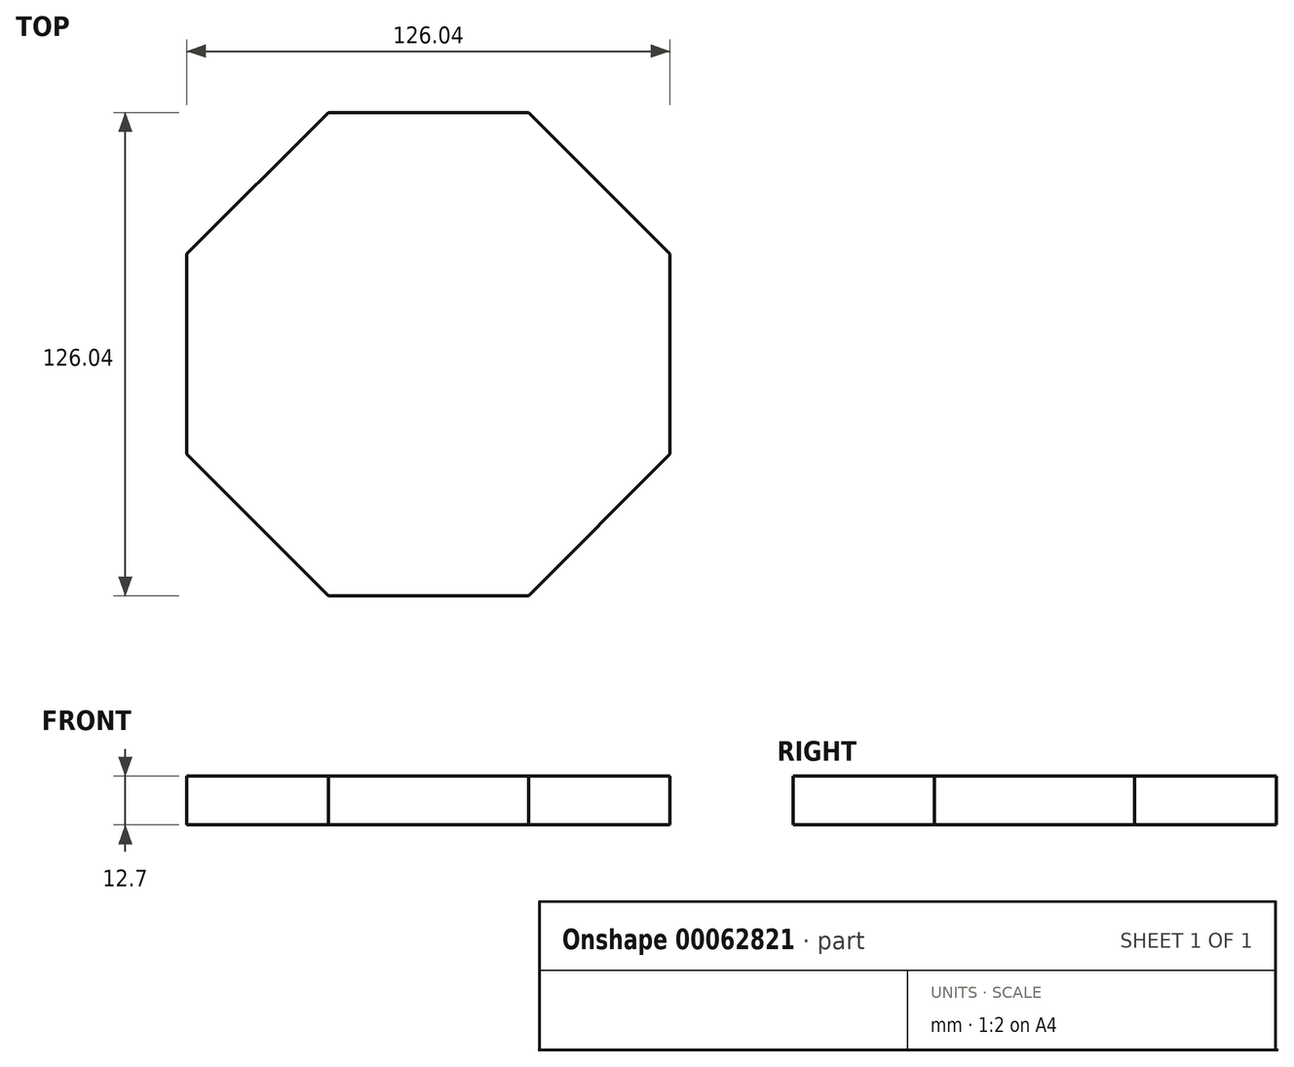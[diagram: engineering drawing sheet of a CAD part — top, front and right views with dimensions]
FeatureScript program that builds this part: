
annotation { "Feature Type Name" : "Feature", "Feature Type Description" : "" }
export const myFeature = defineFeature(function(context is Context, id is Id, definition is map)
    precondition{}
    {
        {
            var Q0;
            Q0=qCreatedBy(makeId("Top.planeOp"),FACE);
            var sketch = newSketch(context, id + "F0", { "sketchPlane" : qUnion([Q0])});
            skLineSegment(sketch, "E0.0", {"start": v(-26.1, 63.02) * mm, "end": v(26.1, 63.02) * mm});
            skLineSegment(sketch, "E0.1", {"start": v(26.1, 63.02) * mm, "end": v(63.02, 26.1) * mm});
            skLineSegment(sketch, "E0.2", {"start": v(63.02, 26.1) * mm, "end": v(63.02, -26.1) * mm});
            skLineSegment(sketch, "E0.3", {"start": v(63.02, -26.1) * mm, "end": v(26.1, -63.02) * mm});
            skLineSegment(sketch, "E0.4", {"start": v(26.1, -63.02) * mm, "end": v(-26.1, -63.02) * mm});
            skLineSegment(sketch, "E0.5", {"start": v(-26.1, -63.02) * mm, "end": v(-63.02, -26.1) * mm});
            skLineSegment(sketch, "E0.6", {"start": v(-63.02, -26.1) * mm, "end": v(-63.02, 26.1) * mm});
            skLineSegment(sketch, "E0.7", {"start": v(-63.02, 26.1) * mm, "end": v(-26.1, 63.02) * mm});
            skPoint(sketch, "E0.0.midPoint", {"position": v(0, 63.02) * mm});
            skLineSegment(sketch, "E1", {"start": v(0, 0) * mm, "end": v(26.1, 63.02) * mm});
            skLineSegment(sketch, "E2", {"start": v(0, 0) * mm, "end": v(-26.1, 63.02) * mm});
            skLineSegment(sketch, "E3", {"start": v(0, 0) * mm, "end": v(-63.02, 26.1) * mm});
            skLineSegment(sketch, "E4", {"start": v(0, 0) * mm, "end": v(-63.02, -26.1) * mm});
            skLineSegment(sketch, "E5", {"start": v(0, 0) * mm, "end": v(-26.1, -63.02) * mm});
            skLineSegment(sketch, "E6", {"start": v(0, 0) * mm, "end": v(26.1, -63.02) * mm});
            skLineSegment(sketch, "E7", {"start": v(0, 0) * mm, "end": v(63.02, -26.1) * mm});
            skLineSegment(sketch, "E8", {"start": v(0, 0) * mm, "end": v(63.02, 26.1) * mm});
            skPoint(sketch, "E9.centerSnap0", {"position": v(13.05, 31.5) * mm});
            skSolve(sketch);
        }
        {
            var Q0;
            {var subQ4=sQuery(id+"F0.wireOp",EDGE,"E0.5");Q0=makeQuery(id+"F0.imprint","IMPRINT",FACE,{"disambiguationData":[TD([[makeQuery(id+"F0.imprint","IMPRINT",EDGE,{"derivedFrom":subQ4}),-1.0]])]});}
            var Q1;
            {var subQ2=sQuery(id+"F0.wireOp",EDGE,"E0.0");Q1=makeQuery(id+"F0.imprint","IMPRINT",FACE,{"disambiguationData":[TD([[makeQuery(id+"F0.imprint","IMPRINT",EDGE,{"derivedFrom":subQ2}),-1.0]])]});}
            var Q2;
            {var subQ5=sQuery(id+"F0.wireOp",EDGE,"E0.1");Q2=makeQuery(id+"F0.imprint","IMPRINT",FACE,{"disambiguationData":[TD([[makeQuery(id+"F0.imprint","IMPRINT",EDGE,{"derivedFrom":subQ5}),-1.0]])]});}
            var Q3;
            {var subQ5=sQuery(id+"F0.wireOp",EDGE,"E0.2");Q3=makeQuery(id+"F0.imprint","IMPRINT",FACE,{"disambiguationData":[TD([[makeQuery(id+"F0.imprint","IMPRINT",EDGE,{"derivedFrom":subQ5}),-1.0]])]});}
            var Q4;
            {var subQ1=sQuery(id+"F0.wireOp",EDGE,"E0.3");Q4=makeQuery(id+"F0.imprint","IMPRINT",FACE,{"disambiguationData":[TD([[makeQuery(id+"F0.imprint","IMPRINT",EDGE,{"derivedFrom":subQ1}),-1.0]])]});}
            var Q5;
            Q5=makeQuery(id+"F0.imprint","IMPRINT",FACE,{"disambiguationData":[TD([[makeQuery(id+"F0.imprint","IMPRINT",EDGE,{"derivedFrom":sQuery(id+"F0.wireOp",EDGE,"E0.4")}),-1.0]])]});
            var Q6;
            {var subQ1=sQuery(id+"F0.wireOp",EDGE,"E0.6");Q6=makeQuery(id+"F0.imprint","IMPRINT",FACE,{"disambiguationData":[TD([[makeQuery(id+"F0.imprint","IMPRINT",EDGE,{"derivedFrom":subQ1}),-1.0]])]});}
            var Q7;
            {var subQ5=sQuery(id+"F0.wireOp",EDGE,"E0.7");Q7=makeQuery(id+"F0.imprint","IMPRINT",FACE,{"disambiguationData":[TD([[makeQuery(id+"F0.imprint","IMPRINT",EDGE,{"derivedFrom":subQ5}),-1.0]])]});}
            extrude(context, id + "F1", {"entities" : qUnion([Q0, Q1, Q2, Q3, Q4, Q5, Q6, Q7]), "depth" : 12.7 * mm});
        }
    });
